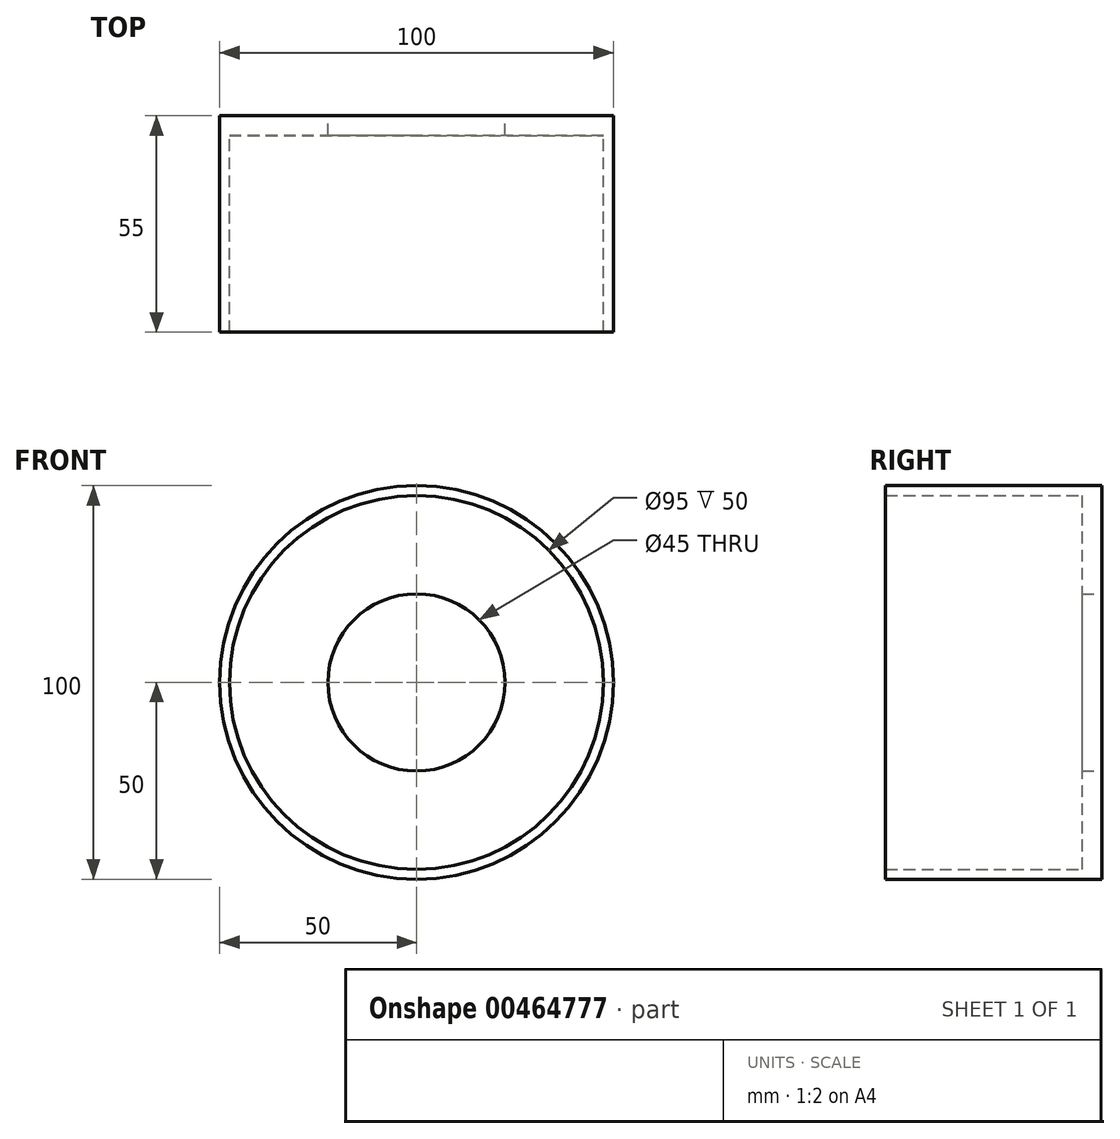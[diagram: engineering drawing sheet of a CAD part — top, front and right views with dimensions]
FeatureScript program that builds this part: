
annotation { "Feature Type Name" : "Feature", "Feature Type Description" : "" }
export const myFeature = defineFeature(function(context is Context, id is Id, definition is map)
    precondition{}
    {
        {
            var Q0;
            Q0=qCreatedBy(makeId("Front.planeOp"),FACE);
            var sketch = newSketch(context, id + "F0", { "sketchPlane" : qUnion([Q0])});
            skCircle(sketch, "E0", {"center": v(0, 0) * mm, "radius": 50 * mm});
            skSolve(sketch);
        }
        {
            var Q0;
            Q0 = qSketchRegion(id + "F0", true);
            extrude(context, id + "F1", {"entities" : qUnion([Q0]), "oppositeDirection" : true, "depth" : 5 * mm});
        }
        {
            var Q0;
            Q0=qCreatedBy(makeId("Front.planeOp"),FACE);
            var sketch = newSketch(context, id + "F2", { "sketchPlane" : qUnion([Q0])});
            skCircle(sketch, "E1", {"center": v(0, 0) * mm, "radius": 50 * mm});
            skCircle(sketch, "E2", {"center": v(0, 0) * mm, "radius": 47.5 * mm});
            skSolve(sketch);
        }
        {
            var Q0;
            Q0 = qSketchRegion(id + "F2", true);
            extrude(context, id + "F3", {"entities" : qUnion([Q0]), "operationType" : NewBodyOperationType.ADD, "depth" : 50 * mm});
        }
        {
            var Q0;
            Q0=makeQuery(id+"F1.opExtrude","CAP_FACE",FACE,{"disambiguationData":[OSD([sQuery(id+"F0.wireOp",EDGE,"E0")])],"isStart":false});
            var sketch = newSketch(context, id + "F4", { "sketchPlane" : qUnion([Q0])});
            skCircle(sketch, "E3", {"center": v(0, 0) * mm, "radius": 25 * mm});
            skCircle(sketch, "E4", {"center": v(0, 0) * mm, "radius": 22.5 * mm});
            skSolve(sketch);
        }
        {
            var Q0;
            Q0=sQuery(id+"F4.wireOp",EDGE,"E4");
            var Q1;
            Q1=sQuery(id+"F4.wireOp",EDGE,"E3");
            extrude(context, id + "F5", {"bodyType" : ToolBodyType.SURFACE, "surfaceEntities" : qUnion([Q0, Q1]), "depth" : 50 * mm});
        }
        {
            var Q0;
            Q0=makeQuery(id+"F4.imprint","IMPRINT",FACE,{"disambiguationData":[TD([[makeQuery(id+"F4.imprint","IMPRINT",EDGE,{"derivedFrom":sQuery(id+"F4.wireOp",EDGE,"E4")}),1.0]])]});
            extrude(context, id + "F6", {"entities" : qUnion([Q0]), "operationType" : NewBodyOperationType.REMOVE, "endBound" : BoundingType.THROUGH_ALL, "oppositeDirection" : true, "depth" : 25 * mm});
        }
    });
